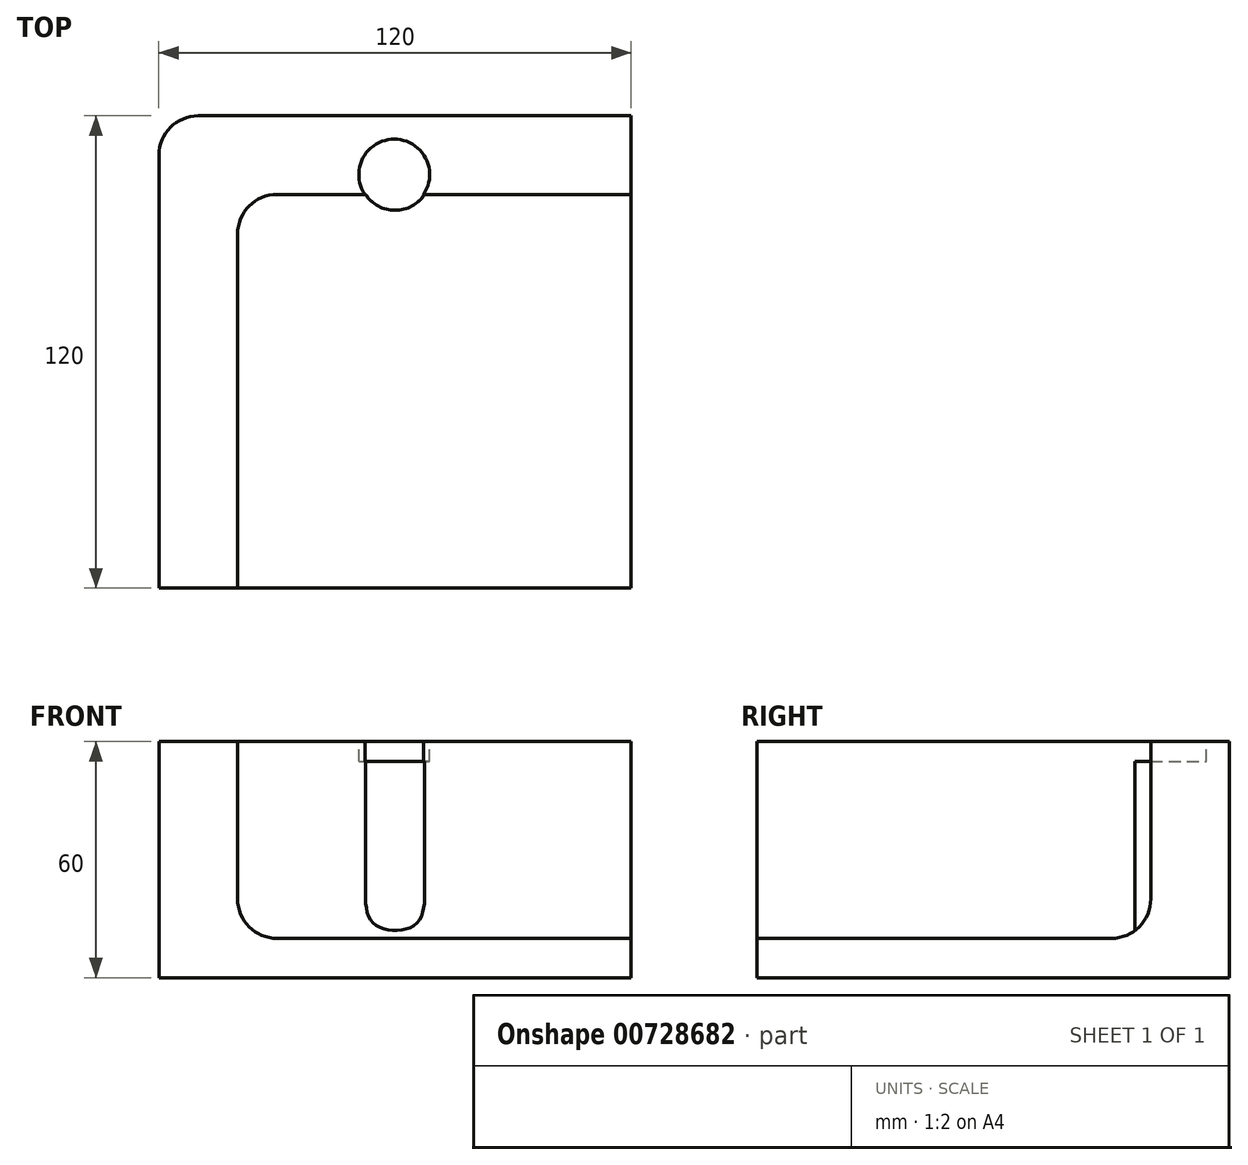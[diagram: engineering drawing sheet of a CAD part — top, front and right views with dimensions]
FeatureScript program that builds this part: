
annotation { "Feature Type Name" : "Feature", "Feature Type Description" : "" }
export const myFeature = defineFeature(function(context is Context, id is Id, definition is map)
    precondition{}
    {
        {
            var Q0;
            Q0=qCreatedBy(makeId("Top.planeOp"),FACE);
            var sketch = newSketch(context, id + "F0", { "sketchPlane" : qUnion([Q0])});
            skLineSegment(sketch, "E0.bottom", {"start": v(-123.33, 4.93) * mm, "end": v(-3.33, 4.93) * mm});
            skLineSegment(sketch, "E0.top", {"start": v(-123.33, -115.07) * mm, "end": v(-3.33, -115.07) * mm});
            skLineSegment(sketch, "E0.left", {"start": v(-123.33, 4.93) * mm, "end": v(-123.33, -115.07) * mm});
            skLineSegment(sketch, "E0.right", {"start": v(-3.33, 4.93) * mm, "end": v(-3.33, -115.07) * mm});
            skSolve(sketch);
        }
        {
            var Q0;
            Q0 = qSketchRegion(id + "F0", true);
            extrude(context, id + "F1", {"entities" : qUnion([Q0]), "depth" : 60 * mm, "offsetDistance" : 25 * mm});
        }
        {
            var Q0;
            Q0=makeQuery(id+"F1.opExtrude","CAP_FACE",FACE,{"disambiguationData":[OSD([sQuery(id+"F0.wireOp",EDGE,"E0.bottom"),sQuery(id+"F0.wireOp",EDGE,"E0.top"),sQuery(id+"F0.wireOp",EDGE,"E0.left"),sQuery(id+"F0.wireOp",EDGE,"E0.right")])],"isStart":false});
            var sketch = newSketch(context, id + "F2", { "sketchPlane" : qUnion([Q0])});
            skLineSegment(sketch, "E1.bottom", {"start": v(-103.33, -15.07) * mm, "end": v(-3.33, -15.07) * mm});
            skLineSegment(sketch, "E1.top", {"start": v(-103.33, -115.07) * mm, "end": v(-3.33, -115.07) * mm});
            skLineSegment(sketch, "E1.left", {"start": v(-103.33, -15.07) * mm, "end": v(-103.33, -115.07) * mm});
            skLineSegment(sketch, "E1.right", {"start": v(-3.33, -15.07) * mm, "end": v(-3.33, -115.07) * mm});
            skSolve(sketch);
        }
        {
            var Q0;
            Q0 = qSketchRegion(id + "F2", true);
            extrude(context, id + "F3", {"entities" : qUnion([Q0]), "operationType" : NewBodyOperationType.REMOVE, "oppositeDirection" : true, "depth" : 50 * mm, "offsetDistance" : 25 * mm});
        }
        {
            var Q0;
            Q0=makeQuery(id+"F3.boolean.opBoolean","COPY",EDGE,{"derivedFrom":makeQuery(id+"F3.opExtrude","SWEPT_EDGE",EDGE,{"disambiguationData":[OSD([sQuery(id+"F2.wireOp",EDGE,"E1.bottom"),sQuery(id+"F2.wireOp",EDGE,"E1.left")])]})});
            var Q1;
            Q1=makeQuery(id+"F3.boolean.opBoolean","COPY",EDGE,{"derivedFrom":makeQuery(id+"F3.opExtrude","CAP_EDGE",EDGE,{"disambiguationData":[OSD([sQuery(id+"F2.wireOp",EDGE,"E1.bottom")])],"isStart":false})});
            var Q2;
            Q2=makeQuery(id+"F3.boolean.opBoolean","COPY",EDGE,{"derivedFrom":makeQuery(id+"F3.opExtrude","CAP_EDGE",EDGE,{"disambiguationData":[OSD([sQuery(id+"F2.wireOp",EDGE,"E1.left")])],"isStart":false})});
            fillet(context, id + "F4", {"entities" : qUnion([Q0, Q1, Q2]), "radius" : 10 * mm, "tangentPropagation" : true, "allowEdgeOverflow" : false});
        }
        {
            var Q0;
            {var subQ4=sQuery(id+"F2.wireOp",EDGE,"E1.bottom");Q0=makeQuery(id+"F2.imprint","IMPRINT",FACE,{"disambiguationData":[TD([[makeQuery(id+"F2.imprint","IMPRINT",EDGE,{"derivedFrom":subQ4}),1.0]])]});}
            var sketch = newSketch(context, id + "F5", { "sketchPlane" : qUnion([Q0])});
            skLineSegment(sketch, "E2", {"start": v(-63.53, -20) * mm, "end": v(-63.53, 0) * mm, "construction": true});
            skLineSegment(sketch, "E3", {"start": v(-3.53, -5) * mm, "end": v(-123.53, -5) * mm, "construction": true});
            skCircle(sketch, "E4", {"center": v(-63.53, -10) * mm, "radius": 9 * mm});
            skSolve(sketch);
        }
        {
            var Q0;
            Q0 = qSketchRegion(id + "F5", true);
            extrude(context, id + "F6", {"entities" : qUnion([Q0]), "operationType" : NewBodyOperationType.REMOVE, "oppositeDirection" : true, "depth" : 5 * mm, "offsetDistance" : 25 * mm});
        }
        {
            var Q0;
            Q0=makeQuery(id+"F1.opExtrude","SWEPT_EDGE",EDGE,{"disambiguationData":[OSD([sQuery(id+"F0.wireOp",EDGE,"E0.bottom"),sQuery(id+"F0.wireOp",EDGE,"E0.left")])]});
            fillet(context, id + "F7", {"entities" : qUnion([Q0]), "radius" : 10 * mm, "tangentPropagation" : true, "allowEdgeOverflow" : false});
        }
        {
            var Q0;
            Q0=makeQuery(id+"F3.boolean.opBoolean","COPY",FACE,{"derivedFrom":makeQuery(id+"F3.opExtrude","CAP_FACE",FACE,{"disambiguationData":[OSD([sQuery(id+"F2.wireOp",EDGE,"E1.bottom"),sQuery(id+"F2.wireOp",EDGE,"E1.top"),sQuery(id+"F2.wireOp",EDGE,"E1.left"),sQuery(id+"F2.wireOp",EDGE,"E1.right")])],"isStart":false})});
            var sketch = newSketch(context, id + "F8", { "sketchPlane" : qUnion([Q0])});
            skLineSegment(sketch, "E5", {"start": v(-3.33, -5.07) * mm, "end": v(-123.33, -5.07) * mm, "construction": true});
            skLineSegment(sketch, "E6", {"start": v(-63.33, -20.07) * mm, "end": v(-63.33, -0.07) * mm});
            skPoint(sketch, "E7", {"position": v(-63.33, -10.07) * mm});
            skCircle(sketch, "E8", {"center": v(-63.33, -10.07) * mm, "radius": 9 * mm});
            skSolve(sketch);
        }
        {
            var Q0;
            Q0 = qSketchRegion(id + "F8", true);
            var Q1;
            Q1=sQuery(id+"F8.wireOp",EDGE,"E8");
            extrude(context, id + "F9", {"entities" : qUnion([Q0]), "operationType" : NewBodyOperationType.ADD, "surfaceEntities" : qUnion([Q1]), "depth" : 45 * mm, "offsetDistance" : 25 * mm});
        }
    });
